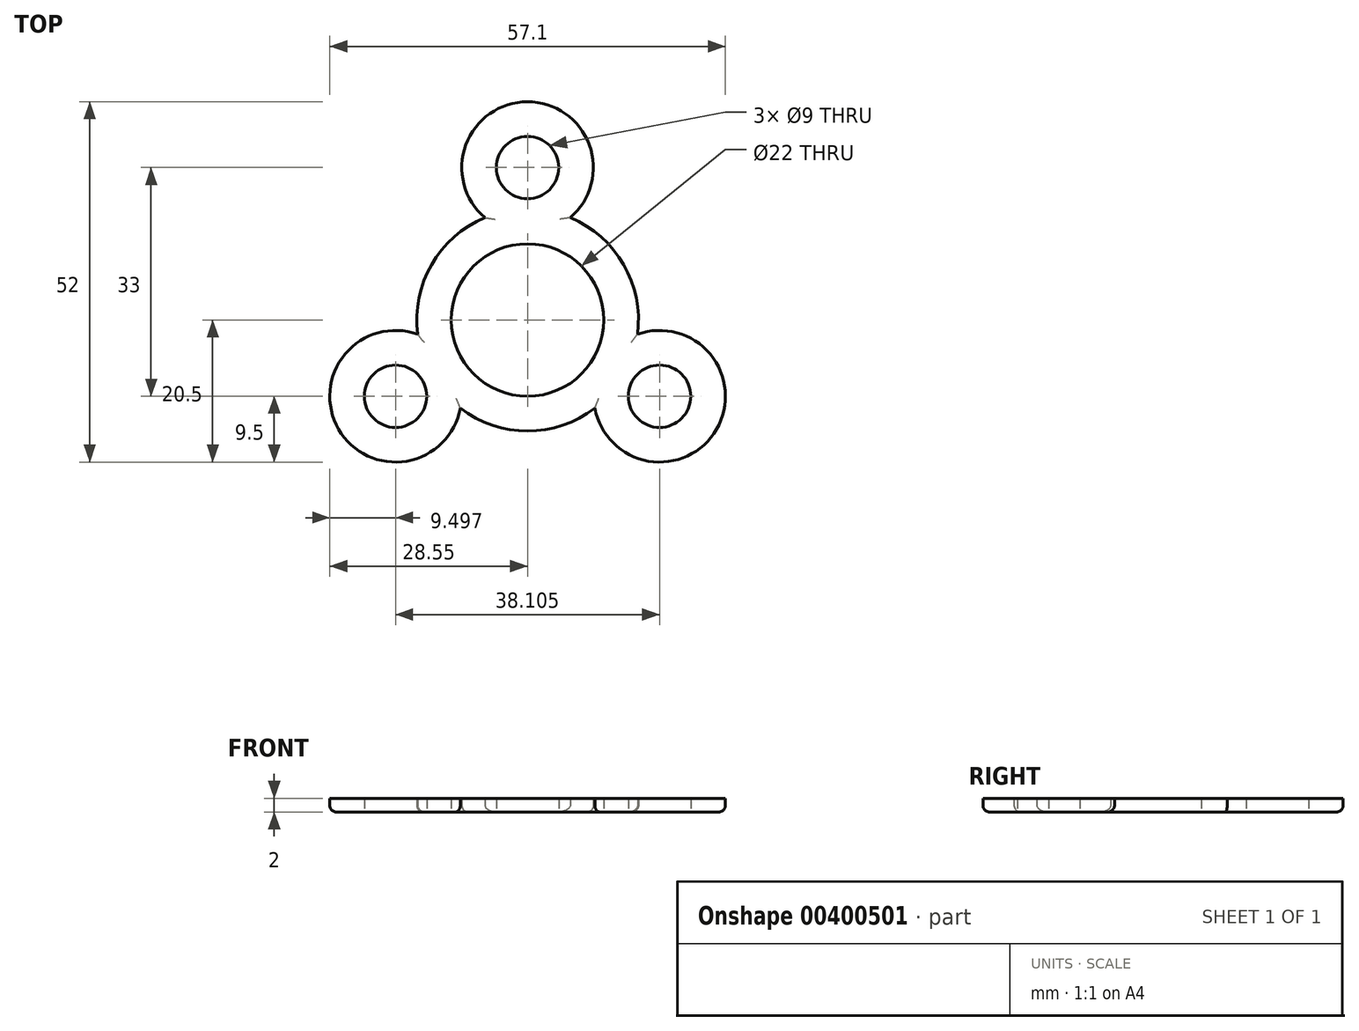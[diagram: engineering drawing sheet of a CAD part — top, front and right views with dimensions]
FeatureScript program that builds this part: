
annotation { "Feature Type Name" : "Feature", "Feature Type Description" : "" }
export const myFeature = defineFeature(function(context is Context, id is Id, definition is map)
    precondition{}
    {
        {
            var Q0;
            Q0=qCreatedBy(makeId("Top.planeOp"),FACE);
            var sketch = newSketch(context, id + "F0", { "sketchPlane" : qUnion([Q0])});
            skLineSegment(sketch, "E0", {"start": v(0, 0) * mm, "end": v(0, 22) * mm, "construction": true});
            skCircle(sketch, "E1", {"center": v(0, 22) * mm, "radius": 9.5 * mm});
            skCircle(sketch, "E2.1.0", {"center": v(-19.05, -11) * mm, "radius": 9.5 * mm});
            skCircle(sketch, "E2.2.0", {"center": v(19.05, -11) * mm, "radius": 9.5 * mm});
            skPoint(sketch, "E2.center", {"position": v(0, 0) * mm});
            skCircle(sketch, "E3.0", {"center": v(0, 0) * mm, "radius": 11 * mm});
            skCircle(sketch, "E4.0", {"center": v(0, 0) * mm, "radius": 16 * mm});
            skCircle(sketch, "E5.0", {"center": v(0, 22) * mm, "radius": 4.5 * mm});
            skCircle(sketch, "E6.1.0", {"center": v(-19.05, -11) * mm, "radius": 4.5 * mm});
            skCircle(sketch, "E6.2.0", {"center": v(19.05, -11) * mm, "radius": 4.5 * mm});
            skSolve(sketch);
        }
        {
            var Q0;
            Q0=qSketchRegion(id+"F0",true);
            extrude(context, id + "F1", {"entities" : qUnion([Q0]), "depth" : 2 * mm});
        }
        {
            var Q0;
            Q0=makeQuery(id+"F1.opExtrude","CAP_EDGE",EDGE,{"disambiguationData":[OSD([sQuery(id+"F0.wireOp",EDGE,"E2.1.0")])],"isStart":true});
            var Q1;
            {var subQ0=sQuery(id+"F0.wireOp",EDGE,"E4.0");Q1=makeQuery(id+"F1.opExtrude","CAP_EDGE",EDGE,{"disambiguationData":[OSD([subQ0]),TDD([makeQuery(id+"F0.imprint","IMPRINT",EDGE,{"disambiguationData":[TD([[makeQuery(id+"F0.imprint","INTERSECT",VERTEX,{"disambiguationData":[OD(1.0)],"derivedFrom":[sQuery(id+"F0.wireOp",EDGE,"E2.1.0"),subQ0]}),-1.0]])],"derivedFrom":subQ0})])],"isStart":true});}
            var Q2;
            Q2=makeQuery(id+"F1.opExtrude","CAP_EDGE",EDGE,{"disambiguationData":[OSD([sQuery(id+"F0.wireOp",EDGE,"E2.2.0")])],"isStart":true});
            var Q3;
            {var subQ0=sQuery(id+"F0.wireOp",EDGE,"E4.0");Q3=makeQuery(id+"F1.opExtrude","CAP_EDGE",EDGE,{"disambiguationData":[OSD([subQ0]),TDD([makeQuery(id+"F0.imprint","IMPRINT",EDGE,{"disambiguationData":[TD([[makeQuery(id+"F0.imprint","INTERSECT",VERTEX,{"disambiguationData":[OD(1.0)],"derivedFrom":[sQuery(id+"F0.wireOp",EDGE,"E1"),subQ0]}),1.0]])],"derivedFrom":subQ0})])],"isStart":true});}
            var Q4;
            Q4=makeQuery(id+"F1.opExtrude","CAP_EDGE",EDGE,{"disambiguationData":[OSD([sQuery(id+"F0.wireOp",EDGE,"E1")])],"isStart":true});
            var Q5;
            {var subQ0=sQuery(id+"F0.wireOp",EDGE,"E4.0");Q5=makeQuery(id+"F1.opExtrude","CAP_EDGE",EDGE,{"disambiguationData":[OSD([subQ0]),TDD([makeQuery(id+"F0.imprint","IMPRINT",EDGE,{"disambiguationData":[TD([[makeQuery(id+"F0.imprint","INTERSECT",VERTEX,{"disambiguationData":[OD(0.0)],"derivedFrom":[sQuery(id+"F0.wireOp",EDGE,"E1"),subQ0]}),-1.0]])],"derivedFrom":subQ0})])],"isStart":true});}
            fillet(context, id + "F2", {"entities" : qUnion([Q0, Q1, Q2, Q3, Q4, Q5]), "radius" : 1 * mm, "tangentPropagation" : true, "allowEdgeOverflow" : false});
        }
        {
            var Q0;
            Q0=makeQuery(id+"F1.opExtrude","SWEPT_BODY",BODY,{"disambiguationData":[OSD([sQuery(id+"F0.wireOp",EDGE,"E1"),sQuery(id+"F0.wireOp",EDGE,"E2.1.0"),sQuery(id+"F0.wireOp",EDGE,"E2.2.0"),sQuery(id+"F0.wireOp",EDGE,"E3.0"),sQuery(id+"F0.wireOp",EDGE,"E4.0"),sQuery(id+"F0.wireOp",EDGE,"E5.0"),sQuery(id+"F0.wireOp",EDGE,"E6.1.0"),sQuery(id+"F0.wireOp",EDGE,"E6.2.0")])]});
            transform(context, id + "F3", {"entities" : qUnion([Q0]), "transformType" : TransformType.TRANSLATION_3D, "dx" : 0 * mm, "dy" : 0 * mm, "dz" : 10 * mm, "makeCopy" : true});
        }
        {
            var Q0;
            Q0=makeQuery(id+"F3.opPattern","COPY",BODY,{"derivedFrom":makeQuery(id+"F1.opExtrude","SWEPT_BODY",BODY,{"disambiguationData":[OSD([sQuery(id+"F0.wireOp",EDGE,"E1"),sQuery(id+"F0.wireOp",EDGE,"E2.1.0"),sQuery(id+"F0.wireOp",EDGE,"E2.2.0"),sQuery(id+"F0.wireOp",EDGE,"E3.0"),sQuery(id+"F0.wireOp",EDGE,"E4.0"),sQuery(id+"F0.wireOp",EDGE,"E5.0"),sQuery(id+"F0.wireOp",EDGE,"E6.1.0"),sQuery(id+"F0.wireOp",EDGE,"E6.2.0")])]}),"instanceName":"1"});
            deleteBodies(context, id + "F4", {"entities" : qUnion([Q0])});
        }
    });
